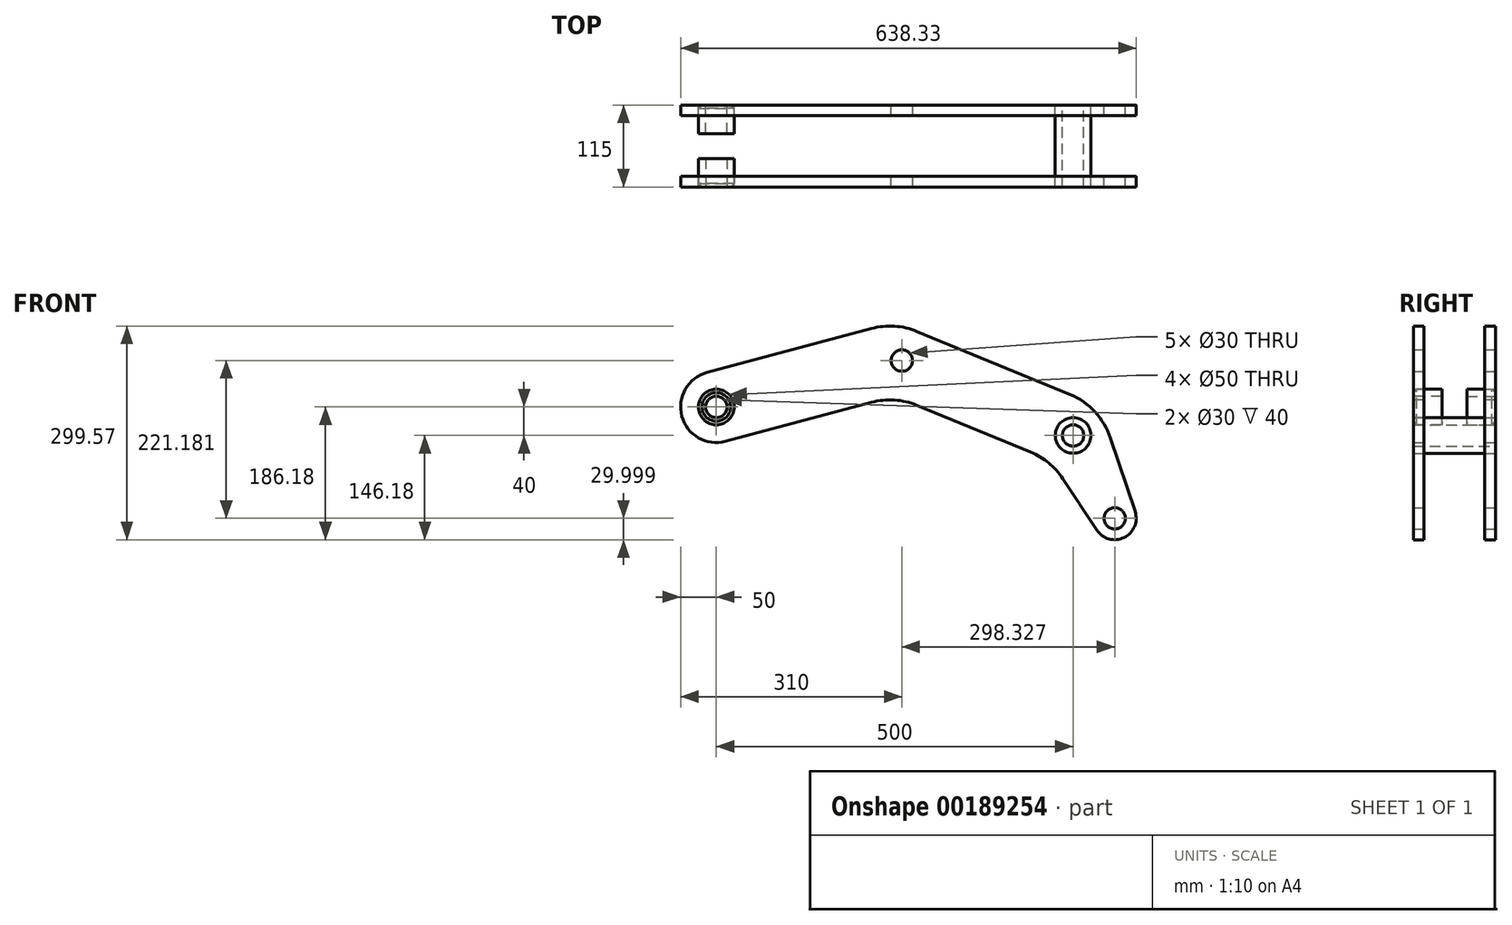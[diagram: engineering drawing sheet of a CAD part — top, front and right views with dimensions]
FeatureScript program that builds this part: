
annotation { "Feature Type Name" : "Feature", "Feature Type Description" : "" }
export const myFeature = defineFeature(function(context is Context, id is Id, definition is map)
    precondition{}
    {
        {
            var Q0;
            Q0=qCreatedBy(makeId("Front.planeOp"),FACE);
            var sketch = newSketch(context, id + "F0", { "sketchPlane" : qUnion([Q0])});
            skCircle(sketch, "E0", {"center": v(0, 0) * mm, "radius": 25 * mm});
            skArc(sketch, "E1", {"start": v(-12.94, 48.3) * mm, "mid": v(-48.3, -12.94) * mm, "end": v(12.94, -48.3) * mm});
            skLineSegment(sketch, "E2", {"start": v(-12.94, 48.3) * mm, "end": v(250, 118.75) * mm});
            skLineSegment(sketch, "E3", {"start": v(12.94, -48.3) * mm, "end": v(250, 15.22) * mm});
            skLineSegment(sketch, "E4", {"start": v(250, 118.75) * mm, "end": v(537.75, 0) * mm});
            skLineSegment(sketch, "E5", {"start": v(250, 15.22) * mm, "end": v(468.67, -75.02) * mm});
            skCircle(sketch, "E6", {"center": v(500, -40) * mm, "radius": 25 * mm});
            skLineSegment(sketch, "E7", {"start": v(468.67, -75.02) * mm, "end": v(533.3, -172.73) * mm});
            skLineSegment(sketch, "E8", {"start": v(537.75, 0) * mm, "end": v(586.78, -146.67) * mm});
            skLineSegment(sketch, "E9", {"start": v(500, -40) * mm, "end": v(537.75, 0) * mm, "construction": true});
            skLineSegment(sketch, "E10", {"start": v(0, 0) * mm, "end": v(248.92, 0) * mm, "construction": true});
            skArc(sketch, "E11", {"start": v(533.3, -172.73) * mm, "mid": v(571.47, -183.15) * mm, "end": v(586.78, -146.67) * mm});
            skLineSegment(sketch, "E12", {"start": v(500, -40) * mm, "end": v(558.33, -156.18) * mm, "construction": true});
            skCircle(sketch, "E13", {"center": v(558.33, -156.18) * mm, "radius": 15 * mm});
            skCircle(sketch, "E14", {"center": v(260, 65) * mm, "radius": 15 * mm});
            skSolve(sketch);
        }
        {
            var Q0;
            Q0 = qSketchRegion(id + "F0", true);
            extrude(context, id + "F1", {"entities" : qUnion([Q0]), "depth" : 7.5 * mm, "hasSecondDirection" : true, "secondDirectionOppositeDirection" : true, "secondDirectionDepth" : 7.5 * mm});
        }
        {
            var Q0;
            Q0=makeQuery(id+"F1.opExtrude","SWEPT_EDGE",EDGE,{"disambiguationData":[OSD([sQuery(id+"F0.wireOp",EDGE,"E2"),sQuery(id+"F0.wireOp",EDGE,"E4")])]});
            var Q1;
            Q1=makeQuery(id+"F1.opExtrude","SWEPT_EDGE",EDGE,{"disambiguationData":[OSD([sQuery(id+"F0.wireOp",EDGE,"E4"),sQuery(id+"F0.wireOp",EDGE,"E8")])]});
            fillet(context, id + "F2", {"entities" : qUnion([Q0, Q1]), "radius" : 100 * mm, "tangentPropagation" : true, "allowEdgeOverflow" : false});
        }
        {
            var Q0;
            Q0=makeQuery(id+"F1.opExtrude","SWEPT_EDGE",EDGE,{"disambiguationData":[OSD([sQuery(id+"F0.wireOp",EDGE,"E3"),sQuery(id+"F0.wireOp",EDGE,"E5")])]});
            var Q1;
            Q1=makeQuery(id+"F1.opExtrude","SWEPT_EDGE",EDGE,{"disambiguationData":[OSD([sQuery(id+"F0.wireOp",EDGE,"E5"),sQuery(id+"F0.wireOp",EDGE,"E7")])]});
            fillet(context, id + "F3", {"entities" : qUnion([Q0, Q1]), "radius" : 100 * mm, "tangentPropagation" : true, "allowEdgeOverflow" : false});
        }
        {
            var Q0;
            Q0=makeQuery(id+"F1.opExtrude","SWEPT_BODY",BODY,{"disambiguationData":[OSD([sQuery(id+"F0.wireOp",EDGE,"E0"),sQuery(id+"F0.wireOp",EDGE,"E1"),sQuery(id+"F0.wireOp",EDGE,"E2"),sQuery(id+"F0.wireOp",EDGE,"E3"),sQuery(id+"F0.wireOp",EDGE,"E4"),sQuery(id+"F0.wireOp",EDGE,"E5"),sQuery(id+"F0.wireOp",EDGE,"cc4923e1-3566-4bcc-90f8-33426ecd6ff4"),sQuery(id+"F0.wireOp",EDGE,"E6")])]});
            var Q1;
            Q1=makeQuery(id+"F1.opExtrude","CAP_FACE",FACE,{"disambiguationData":[OSD([sQuery(id+"F0.wireOp",EDGE,"E0"),sQuery(id+"F0.wireOp",EDGE,"E1"),sQuery(id+"F0.wireOp",EDGE,"E2"),sQuery(id+"F0.wireOp",EDGE,"E3"),sQuery(id+"F0.wireOp",EDGE,"E4"),sQuery(id+"F0.wireOp",EDGE,"E5"),sQuery(id+"F0.wireOp",EDGE,"cc4923e1-3566-4bcc-90f8-33426ecd6ff4"),sQuery(id+"F0.wireOp",EDGE,"E6")])],"isStart":false});
            transform(context, id + "F4", {"entities" : qUnion([Q0]), "transformType" : TransformType.TRANSLATION_DISTANCE, "transformDirection" : qUnion([Q1]), "distance" : 100 * mm, "makeCopy" : true});
        }
        {
            var Q0;
            Q0=makeQuery(id+"F1.opExtrude","CAP_FACE",FACE,{"disambiguationData":[OSD([sQuery(id+"F0.wireOp",EDGE,"E0"),sQuery(id+"F0.wireOp",EDGE,"E1"),sQuery(id+"F0.wireOp",EDGE,"E2"),sQuery(id+"F0.wireOp",EDGE,"E3"),sQuery(id+"F0.wireOp",EDGE,"E4"),sQuery(id+"F0.wireOp",EDGE,"E5"),sQuery(id+"F0.wireOp",EDGE,"cc4923e1-3566-4bcc-90f8-33426ecd6ff4"),sQuery(id+"F0.wireOp",EDGE,"E6")])],"isStart":true});
            var sketch = newSketch(context, id + "F5", { "sketchPlane" : qUnion([Q0])});
            skCircle(sketch, "E15.0", {"center": v(-500, -40) * mm, "radius": 25 * mm});
            skCircle(sketch, "E16", {"center": v(-500, -40) * mm, "radius": 15 * mm});
            skSolve(sketch);
        }
        {
            var Q0;
            Q0 = qSketchRegion(id + "F5", true);
            var Q1;
            Q1=makeQuery(id+"F4.opPattern","COPY",FACE,{"derivedFrom":makeQuery(id+"F1.opExtrude","CAP_FACE",FACE,{"disambiguationData":[OSD([sQuery(id+"F0.wireOp",EDGE,"E0"),sQuery(id+"F0.wireOp",EDGE,"E1"),sQuery(id+"F0.wireOp",EDGE,"E2"),sQuery(id+"F0.wireOp",EDGE,"E3"),sQuery(id+"F0.wireOp",EDGE,"E4"),sQuery(id+"F0.wireOp",EDGE,"E5"),sQuery(id+"F0.wireOp",EDGE,"cc4923e1-3566-4bcc-90f8-33426ecd6ff4"),sQuery(id+"F0.wireOp",EDGE,"E6")])],"isStart":false}),"instanceName":"1"});
            extrude(context, id + "F6", {"entities" : qUnion([Q0]), "endBound" : BoundingType.UP_TO_SURFACE, "oppositeDirection" : true, "endBoundEntityFace" : qUnion([Q1]), "depth" : 25 * mm});
        }
        {
            var Q0;
            Q0=makeQuery(id+"F4.opPattern","COPY",FACE,{"derivedFrom":makeQuery(id+"F1.opExtrude","CAP_FACE",FACE,{"disambiguationData":[OSD([sQuery(id+"F0.wireOp",EDGE,"E0"),sQuery(id+"F0.wireOp",EDGE,"E1"),sQuery(id+"F0.wireOp",EDGE,"E2"),sQuery(id+"F0.wireOp",EDGE,"E3"),sQuery(id+"F0.wireOp",EDGE,"E4"),sQuery(id+"F0.wireOp",EDGE,"E5"),sQuery(id+"F0.wireOp",EDGE,"E6"),sQuery(id+"F0.wireOp",EDGE,"E7"),sQuery(id+"F0.wireOp",EDGE,"E8"),sQuery(id+"F0.wireOp",EDGE,"E11"),sQuery(id+"F0.wireOp",EDGE,"E13"),sQuery(id+"F0.wireOp",EDGE,"E14")])],"isStart":false}),"instanceName":"1"});
            var sketch = newSketch(context, id + "F7", { "sketchPlane" : qUnion([Q0])});
            skCircle(sketch, "E17.0", {"center": v(0, 0) * mm, "radius": 25 * mm});
            skCircle(sketch, "E18", {"center": v(0, 0) * mm, "radius": 15 * mm});
            skSolve(sketch);
        }
        {
            var Q0;
            Q0=makeQuery(id+"F7.imprint","IMPRINT",FACE,{"disambiguationData":[TD([[makeQuery(id+"F7.imprint","IMPRINT",EDGE,{"derivedFrom":sQuery(id+"F7.wireOp",EDGE,"E17.0")}),1.0]])]});
            extrude(context, id + "F8", {"entities" : qUnion([Q0]), "oppositeDirection" : true, "depth" : 40 * mm});
        }
        {
            var Q0;
            Q0=makeQuery(id+"F4.opPattern","COPY",FACE,{"derivedFrom":makeQuery(id+"F1.opExtrude","CAP_FACE",FACE,{"disambiguationData":[OSD([sQuery(id+"F0.wireOp",EDGE,"E0"),sQuery(id+"F0.wireOp",EDGE,"E1"),sQuery(id+"F0.wireOp",EDGE,"E2"),sQuery(id+"F0.wireOp",EDGE,"E3"),sQuery(id+"F0.wireOp",EDGE,"E4"),sQuery(id+"F0.wireOp",EDGE,"E5"),sQuery(id+"F0.wireOp",EDGE,"E6"),sQuery(id+"F0.wireOp",EDGE,"E7"),sQuery(id+"F0.wireOp",EDGE,"E8"),sQuery(id+"F0.wireOp",EDGE,"E11"),sQuery(id+"F0.wireOp",EDGE,"E13"),sQuery(id+"F0.wireOp",EDGE,"E14")])],"isStart":false}),"instanceName":"1"});
            var Q1;
            Q1=makeQuery(id+"F1.opExtrude","CAP_FACE",FACE,{"disambiguationData":[OSD([sQuery(id+"F0.wireOp",EDGE,"E0"),sQuery(id+"F0.wireOp",EDGE,"E1"),sQuery(id+"F0.wireOp",EDGE,"E2"),sQuery(id+"F0.wireOp",EDGE,"E3"),sQuery(id+"F0.wireOp",EDGE,"E4"),sQuery(id+"F0.wireOp",EDGE,"E5"),sQuery(id+"F0.wireOp",EDGE,"E6"),sQuery(id+"F0.wireOp",EDGE,"E7"),sQuery(id+"F0.wireOp",EDGE,"E8"),sQuery(id+"F0.wireOp",EDGE,"E11"),sQuery(id+"F0.wireOp",EDGE,"E13"),sQuery(id+"F0.wireOp",EDGE,"E14")])],"isStart":true});
            cPlane(context, id + "F9", {"entities" : qUnion([Q0, Q1]), "cplaneType" : CPlaneType.MID_PLANE, "offset" : 25 * mm, "width" : 150 * mm, "height" : 150 * mm});
        }
        {
            var Q0;
            Q0=makeQuery(id+"F8.opExtrude","CAP_EDGE",EDGE,{"disambiguationData":[OSD([sQuery(id+"F7.wireOp",EDGE,"E17.0")])],"isStart":true});
            chamfer(context, id + "F10", {"entities" : qUnion([Q0]), "width" : 5 * mm, "tangentPropagation" : true});
        }
        {
            var Q0;
            Q0=makeQuery(id+"F8.opExtrude","SWEPT_BODY",BODY,{"disambiguationData":[OSD([sQuery(id+"F7.wireOp",EDGE,"E17.0"),sQuery(id+"F7.wireOp",EDGE,"E18")])]});
            var Q1;
            Q1=qCreatedBy(id+"F9.planeOp",FACE);
            mirror(context, id + "F11", {"entities" : qUnion([Q0]), "mirrorPlane" : qUnion([Q1])});
        }
    });
